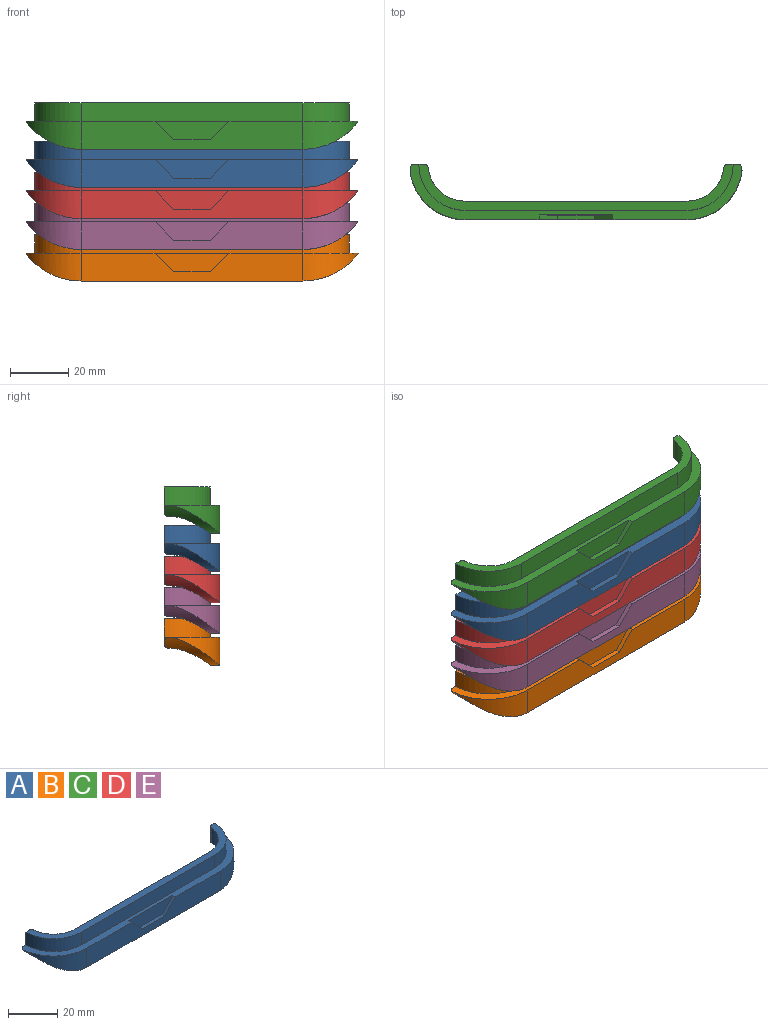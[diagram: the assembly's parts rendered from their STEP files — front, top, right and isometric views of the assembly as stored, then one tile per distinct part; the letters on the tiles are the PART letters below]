
ASSEMBLY  parts=5 mates=8
PART A: 32 faces, bbox 124x19.1x17.4 mm
  f0: plane 9.03x3.19mm, normal (0,1,0), area 16mm2, adj f5,f9,f10,f15,f16,f29,f31
  f1: plane 9.03x3.19mm, normal (0,1,0), area 16mm2, adj f7,f8,f10,f27,f28,f30,f31
  f2: cylinder r=12.7mm len=12.62mm, axis (0,0,-1), area 135.4mm2, adj f4,f9,f14,f16,f31
  f3: cylinder r=12.7mm len=12.62mm, axis (0,0,-1), area 135.4mm2, adj f4,f8,f21,f28,f31
  f4: plane 76.2x7.3mm, normal (0,1,0), area 556.5mm2, adj f2,f3,f22,f31
  f5: cylinder r=15.88mm len=15.88mm, axis (0,0,-1), area 158.3mm2, adj f0,f6,f10,f31
  f6: plane 76.2x6.35mm, normal (0,-1,0), area 483.9mm2, adj f5,f7,f10,f31
  f7: cylinder r=15.88mm len=15.88mm, axis (0,0,-1), area 158.3mm2, adj f1,f6,f10,f31
  f8: cylinder r=1.59mm len=7.3mm, axis (0,0,-1), area 16.2mm2, adj f1,f3,f28,f31
  f9: cylinder r=1.59mm len=7.3mm, axis (0,0,-1), area 16.2mm2, adj f0,f2,f16,f31
  f10: plane 114.03x19.05mm, normal (0,0,1), area 374.5mm2, adj f0,f1,f5,f6,f7,f12,f15,f17
  f11: plane 76.2x3.18mm, normal (0,0,-1), area 241.9mm2, adj f18,f20,f29,f30
  f12: cylinder r=19.05mm len=18.91mm, axis (0,0,-1), area 131.7mm2, adj f10,f18,f29
  f13: cylinder r=15.88mm len=15mm, axis (0,0,-1), area 53mm2, adj f14,f20,f29
  f14: cone r=14.29mm half-angle=45deg, axis (0,0,-1), area 93.1mm2, adj f2,f13,f16,f22,f29
  f15: cylinder r=1.59mm len=1.85mm, axis (0,0,-1), area 1.9mm2, adj f0,f10,f29
  f16: bspline ~13.94x13.89mm, area 8.9mm2, adj f0,f2,f9,f14,f29
  f17: cylinder r=19.05mm len=18.91mm, axis (0,0,-1), area 131.7mm2, adj f10,f18,f30
  f18: plane 76.2x9.53mm, normal (0,-1,0), area 604.8mm2, adj f10,f11,f12,f17,f23,f24,f25
  f19: cylinder r=15.88mm len=15mm, axis (0,0,-1), area 53mm2, adj f20,f21,f30
  f20: plane 76.2x5.4mm, normal (0,1,0), area 411.3mm2, adj f11,f13,f19,f22
  f21: cone r=14.29mm half-angle=45deg, axis (0,0,-1), area 93.1mm2, adj f3,f19,f22,f28,f30
  f22: plane 76.2x3.18mm, normal (0,0.71,-0.71), area 342.1mm2, adj f4,f14,f20,f21
  f23: plane 6.35x6.35mm, normal (0.71,0,0.71), area 14.3mm2, adj f10,f18,f24,f26
  f24: plane 12.7x1.59mm, normal (0,0,1), area 20.2mm2, adj f18,f23,f25,f26
  f25: plane 6.35x6.35mm, normal (-0.71,0,0.71), area 14.3mm2, adj f10,f18,f24,f26
  f26: plane 25.4x6.35mm, normal (0,-1,0), area 121mm2, adj f10,f23,f24,f25
  f27: cylinder r=1.59mm len=1.85mm, axis (0,0,-1), area 1.9mm2, adj f1,f10,f30
  f28: bspline ~13.94x13.89mm, area 8.9mm2, adj f1,f3,f8,f21,f30
  f29: cylinder r=23.54mm len=19.05mm, axis (0,-1,0), area 105mm2, adj f0,f10,f11,f12,f13,f14,f15,f16
  f30: cylinder r=23.54mm len=19.05mm, axis (0,-1,0), area 105mm2, adj f1,f10,f11,f17,f19,f21,f27,f28
  f31: plane 107.95x15.88mm, normal (0,0,1), area 383.5mm2, adj f0,f1,f2,f3,f4,f5,f6,f7
PART B: same geometry as A
PART C: same geometry as A
PART D: same geometry as A
PART E: same geometry as A
PLACE A rot(axis=(-0.07,-1,0.07),0deg) t=(11.89,-16.3,27.46)mm
PLACE B rot(axis=(-0.07,-1,0.07),0deg) t=(11.89,-16.3,-4.71)mm
PLACE C rot(axis=(-0.07,-1,0.07),0deg) t=(11.89,-16.3,40.56)mm
PLACE D rot(axis=(-0.07,-1,0.07),0deg) t=(11.89,-16.3,16.74)mm
PLACE E rot(axis=(-0.07,-1,0.07),0deg) t=(11.89,-16.3,6.12)mm
MATE cylindrical A.f2 <-> E.f2  axis (0,0,-1) through (-26.21,2.75,27.43)mm
MATE planar D.f18 <-> E.f18  axis (0,-1,0) through (-13.51,-16.3,21.5)mm
MATE cylindrical E.f3 <-> D.f3  axis (0,0,-1) through (49.99,2.75,6.09)mm
MATE planar C.f18 <-> E.f18  axis (0,-1,0) through (-13.51,-16.3,45.32)mm
MATE planar C.f18 <-> A.f18  axis (0,-1,0) through (11.89,-16.3,40.17)mm
MATE planar B.f18 <-> D.f18  axis (0,-1,0) through (37.29,-16.3,0.05)mm
MATE cylindrical E.f3 <-> B.f3  axis (0,0,-1) through (49.99,2.75,6.09)mm
MATE cylindrical A.f2 <-> C.f2  axis (0,0,-1) through (-26.21,2.75,27.43)mm
